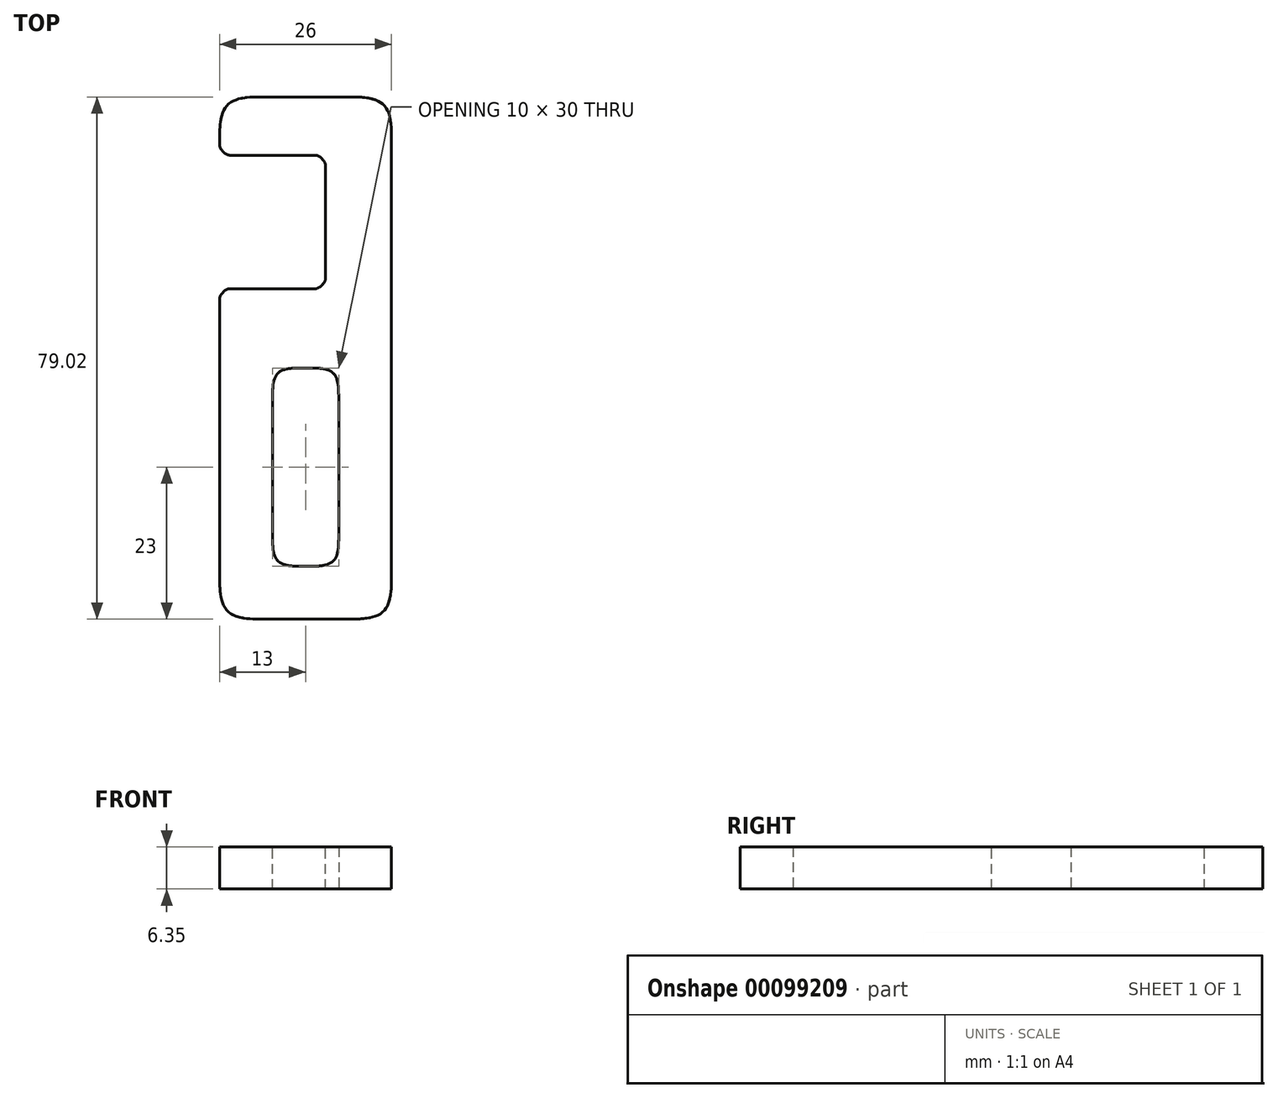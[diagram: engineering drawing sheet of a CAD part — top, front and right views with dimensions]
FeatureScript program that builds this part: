
annotation { "Feature Type Name" : "Feature", "Feature Type Description" : "" }
export const myFeature = defineFeature(function(context is Context, id is Id, definition is map)
    precondition{}
    {
        {
            var Q0;
            Q0=qCreatedBy(makeId("Top.planeOp"),FACE);
            var sketch = newSketch(context, id + "F0", { "sketchPlane" : qUnion([Q0])});
            skLineSegment(sketch, "E0.bottom", {"start": v(0, 0) * mm, "end": v(26, 0) * mm});
            skLineSegment(sketch, "E0.top", {"start": v(0, 79.02) * mm, "end": v(26, 79.02) * mm});
            skLineSegment(sketch, "E0.left", {"start": v(0, 0) * mm, "end": v(0, 50) * mm});
            skLineSegment(sketch, "E0.right", {"start": v(26, 0) * mm, "end": v(26, 79.02) * mm});
            skLineSegment(sketch, "E1.bottom", {"start": v(8, 8) * mm, "end": v(18, 8) * mm});
            skLineSegment(sketch, "E1.top", {"start": v(8, 38) * mm, "end": v(18, 38) * mm});
            skLineSegment(sketch, "E1.left", {"start": v(8, 8) * mm, "end": v(8, 38) * mm});
            skLineSegment(sketch, "E1.right", {"start": v(18, 8) * mm, "end": v(18, 38) * mm});
            skLineSegment(sketch, "E2", {"start": v(0, 70.2) * mm, "end": v(16, 70.2) * mm});
            skLineSegment(sketch, "E3", {"start": v(16, 70.2) * mm, "end": v(16, 50) * mm});
            skLineSegment(sketch, "E4", {"start": v(16, 50) * mm, "end": v(0, 50) * mm});
            skLineSegment(sketch, "E5.trimOffspring", {"start": v(0, 70.2) * mm, "end": v(0, 79.02) * mm});
            skSolve(sketch);
        }
        {
            var Q0;
            Q0 = qSketchRegion(id + "F0", true);
            extrude(context, id + "F1", {"entities" : qUnion([Q0]), "depth" : 6.35 * mm});
        }
        {
            var Q0;
            Q0=makeQuery(id+"F1.opExtrude","SWEPT_EDGE",EDGE,{"disambiguationData":[OSD([sQuery(id+"F0.wireOp",EDGE,"E0.top"),sQuery(id+"F0.wireOp",EDGE,"E0.right")])]});
            var Q1;
            Q1=makeQuery(id+"F1.opExtrude","SWEPT_EDGE",EDGE,{"disambiguationData":[OSD([sQuery(id+"F0.wireOp",EDGE,"E0.top"),sQuery(id+"F0.wireOp",EDGE,"E5.trimOffspring")])]});
            var Q2;
            Q2=makeQuery(id+"F1.opExtrude","SWEPT_EDGE",EDGE,{"disambiguationData":[OSD([sQuery(id+"F0.wireOp",EDGE,"E0.bottom"),sQuery(id+"F0.wireOp",EDGE,"E0.right")])]});
            var Q3;
            Q3=makeQuery(id+"F1.opExtrude","SWEPT_EDGE",EDGE,{"disambiguationData":[OSD([sQuery(id+"F0.wireOp",EDGE,"E0.bottom"),sQuery(id+"F0.wireOp",EDGE,"E0.left")])]});
            fillet(context, id + "F2", {"entities" : qUnion([Q0, Q1, Q2, Q3]), "radius" : 6 * mm, "tangentPropagation" : true, "rho" : .6, "crossSection" : FilletCrossSection.CONIC, "allowEdgeOverflow" : false});
        }
        {
            var Q0;
            Q0=makeQuery(id+"F1.opExtrude","SWEPT_EDGE",EDGE,{"disambiguationData":[OSD([sQuery(id+"F0.wireOp",EDGE,"E2"),sQuery(id+"F0.wireOp",EDGE,"E5.trimOffspring")])]});
            var Q1;
            Q1=makeQuery(id+"F1.opExtrude","SWEPT_EDGE",EDGE,{"disambiguationData":[OSD([sQuery(id+"F0.wireOp",EDGE,"E0.left"),sQuery(id+"F0.wireOp",EDGE,"E4")])]});
            var Q2;
            Q2=makeQuery(id+"F1.opExtrude","SWEPT_EDGE",EDGE,{"disambiguationData":[OSD([sQuery(id+"F0.wireOp",EDGE,"E3"),sQuery(id+"F0.wireOp",EDGE,"E4")])]});
            var Q3;
            Q3=makeQuery(id+"F1.opExtrude","SWEPT_EDGE",EDGE,{"disambiguationData":[OSD([sQuery(id+"F0.wireOp",EDGE,"E2"),sQuery(id+"F0.wireOp",EDGE,"E3")])]});
            fillet(context, id + "F3", {"entities" : qUnion([Q0, Q1, Q2, Q3]), "radius" : 1.5 * mm, "tangentPropagation" : true, "rho" : .3, "crossSection" : FilletCrossSection.CONIC, "allowEdgeOverflow" : false});
        }
        {
            var Q0;
            Q0=makeQuery(id+"F1.opExtrude","SWEPT_EDGE",EDGE,{"disambiguationData":[OSD([sQuery(id+"F0.wireOp",EDGE,"E1.top"),sQuery(id+"F0.wireOp",EDGE,"E1.right")])]});
            var Q1;
            Q1=makeQuery(id+"F1.opExtrude","SWEPT_EDGE",EDGE,{"disambiguationData":[OSD([sQuery(id+"F0.wireOp",EDGE,"E1.top"),sQuery(id+"F0.wireOp",EDGE,"E1.left")])]});
            var Q2;
            Q2=makeQuery(id+"F1.opExtrude","SWEPT_EDGE",EDGE,{"disambiguationData":[OSD([sQuery(id+"F0.wireOp",EDGE,"E1.bottom"),sQuery(id+"F0.wireOp",EDGE,"E1.left")])]});
            var Q3;
            Q3=makeQuery(id+"F1.opExtrude","SWEPT_EDGE",EDGE,{"disambiguationData":[OSD([sQuery(id+"F0.wireOp",EDGE,"E1.bottom"),sQuery(id+"F0.wireOp",EDGE,"E1.right")])]});
            fillet(context, id + "F4", {"entities" : qUnion([Q0, Q1, Q2, Q3]), "radius" : 4 * mm, "tangentPropagation" : true, "rho" : .6, "crossSection" : FilletCrossSection.CONIC, "allowEdgeOverflow" : false});
        }
    });
